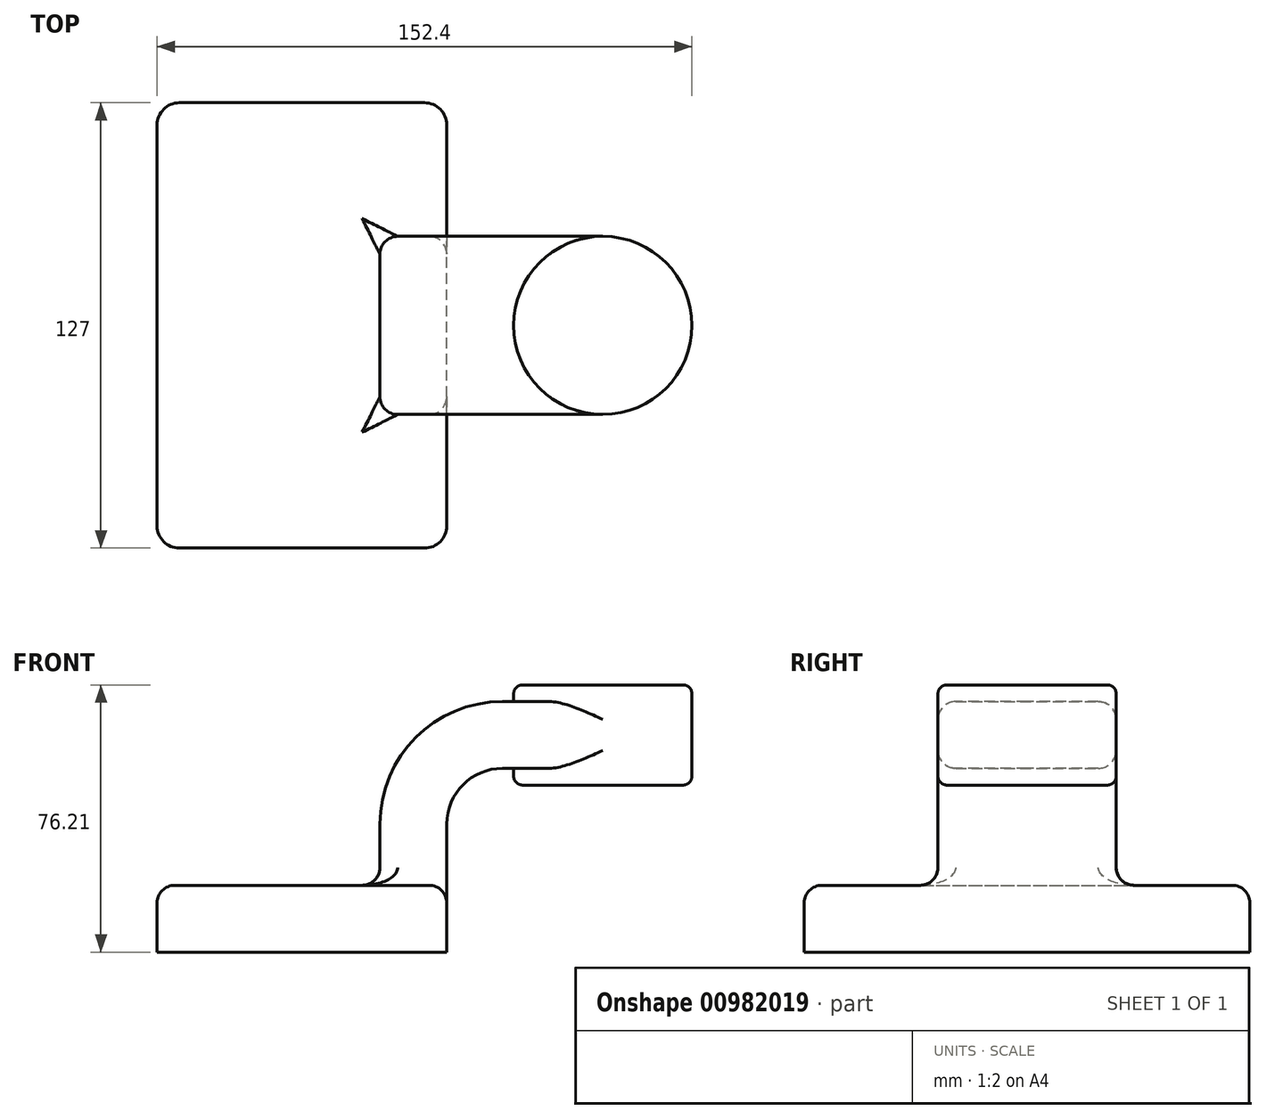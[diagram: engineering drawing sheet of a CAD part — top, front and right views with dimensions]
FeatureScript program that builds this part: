
annotation { "Feature Type Name" : "Feature", "Feature Type Description" : "" }
export const myFeature = defineFeature(function(context is Context, id is Id, definition is map)
    precondition{}
    {
        {
            var Q0;
            Q0=qCreatedBy(makeId("Front.planeOp"),FACE);
            var sketch = newSketch(context, id + "F0", { "sketchPlane" : qUnion([Q0])});
            skLineSegment(sketch, "E0.bottom", {"start": v(-41.28, -9.53) * mm, "end": v(41.28, -9.53) * mm});
            skLineSegment(sketch, "E0.top", {"start": v(-41.28, 9.52) * mm, "end": v(41.28, 9.52) * mm});
            skLineSegment(sketch, "E0.left", {"start": v(-41.28, -9.53) * mm, "end": v(-41.28, 9.52) * mm});
            skLineSegment(sketch, "E0.right", {"start": v(41.28, -9.53) * mm, "end": v(41.28, 9.52) * mm});
            skPoint(sketch, "E0.middle", {"position": v(0, 0) * mm});
            skLineSegment(sketch, "E1.bottom", {"start": v(111.12, 66.68) * mm, "end": v(60.32, 66.68) * mm});
            skLineSegment(sketch, "E1.top", {"start": v(111.12, 38.1) * mm, "end": v(60.32, 38.1) * mm});
            skLineSegment(sketch, "E1.left", {"start": v(111.12, 66.68) * mm, "end": v(111.12, 38.1) * mm});
            skLineSegment(sketch, "E1.right", {"start": v(60.32, 66.67) * mm, "end": v(60.32, 38.1) * mm});
            skPoint(sketch, "E1.middle", {"position": v(85.72, 52.39) * mm});
            skLineSegment(sketch, "E2", {"start": v(41.27, 9.52) * mm, "end": v(41.27, 27) * mm});
            skArc(sketch, "E3", {"start": v(41.27, 27) * mm, "mid": v(45.92, 38.23) * mm, "end": v(57.15, 42.88) * mm});
            skLineSegment(sketch, "E4", {"start": v(57.15, 42.88) * mm, "end": v(85.72, 42.88) * mm});
            skPoint(sketch, "E4.endSnap0", {"position": v(85.72, 38.1) * mm});
            skLineSegment(sketch, "E5.0", {"start": v(57.15, 61.93) * mm, "end": v(85.72, 61.93) * mm});
            skArc(sketch, "E5.1", {"start": v(22.23, 27) * mm, "mid": v(32.45, 51.7) * mm, "end": v(57.15, 61.93) * mm});
            skLineSegment(sketch, "E5.2", {"start": v(22.22, 9.52) * mm, "end": v(22.22, 27) * mm});
            skLineSegment(sketch, "E6", {"start": v(85.72, 66.68) * mm, "end": v(85.72, 38.1) * mm});
            skFitSpline(sketch, "E7", {"points": [v(-41.28, 9.53) * mm, v(57.15, 61.93) * mm], "startDerivative": vector(29.37, 69.56) * mm, "endDerivative": vector(135.05, -5.43) * mm});
            skSolve(sketch);
        }
        {
            var Q0;
            Q0=makeQuery(id+"F0.imprint","IMPRINT",FACE,{"disambiguationData":[TD([[makeQuery(id+"F0.imprint","IMPRINT",EDGE,{"derivedFrom":sQuery(id+"F0.wireOp",EDGE,"E0.bottom")}),1.0]])]});
            extrude(context, id + "F1", {"entities" : qUnion([Q0]), "endBound" : BoundingType.SYMMETRIC, "depth" : 127 * mm, "offsetDistance" : 25.4 * mm});
        }
        {
            var Q0;
            {var subQ1=sQuery(id+"F0.wireOp",EDGE,"E2");Q0=makeQuery(id+"F0.imprint","IMPRINT",FACE,{"disambiguationData":[TD([[makeQuery(id+"F0.imprint","IMPRINT",EDGE,{"derivedFrom":subQ1}),1.0]])]});}
            var Q1;
            {var subQ0=sQuery(id+"F0.wireOp",EDGE,"E5.0");var subQ1=sQuery(id+"F0.wireOp",EDGE,"E1.right");var subQ2=makeQuery(id+"F0.imprint","INTERSECT",VERTEX,{"derivedFrom":[subQ1,subQ0]});Q1=makeQuery(id+"F0.imprint","IMPRINT",FACE,{"disambiguationData":[TD([[makeQuery(id+"F0.imprint","IMPRINT",EDGE,{"disambiguationData":[TD([[subQ2,-1.0]])],"derivedFrom":subQ1}),1.0]])]});}
            extrude(context, id + "F2", {"entities" : qUnion([Q0, Q1]), "operationType" : NewBodyOperationType.ADD, "endBound" : BoundingType.SYMMETRIC, "depth" : 50.8 * mm, "offsetDistance" : 25.4 * mm});
        }
        {
            var Q0;
            Q0=makeQuery(id+"F0.imprint","IMPRINT",FACE,{"disambiguationData":[TD([[makeQuery(id+"F0.imprint","IMPRINT",EDGE,{"derivedFrom":sQuery(id+"F0.wireOp",EDGE,"E5.1")}),1.0]])]});
            extrude(context, id + "F3", {"entities" : qUnion([Q0]), "operationType" : NewBodyOperationType.ADD, "endBound" : BoundingType.SYMMETRIC, "depth" : 15.88 * mm, "offsetDistance" : 25.4 * mm});
        }
        {
            var Q0;
            {var subQ4=sQuery(id+"F0.wireOp",EDGE,"E1.left");Q0=makeQuery(id+"F0.imprint","IMPRINT",FACE,{"disambiguationData":[TD([[makeQuery(id+"F0.imprint","IMPRINT",EDGE,{"derivedFrom":subQ4}),-1.0]])]});}
            var Q1;
            Q1=sQuery(id+"F0.wireOp",EDGE,"E6");
            revolve(context, id + "F4", {"operationType" : NewBodyOperationType.ADD, "surfaceOperationType" : NewSurfaceOperationType.NEW, "entities" : qUnion([Q0]), "axis" : qUnion([Q1]), "revolveType" : RevolveType.FULL});
        }
        {
            var Q0;
            Q0=makeQuery(id+"F1.opExtrude","CAP_EDGE",EDGE,{"disambiguationData":[OSD([sQuery(id+"F0.wireOp",EDGE,"E0.right")])],"isStart":false});
            var Q1;
            Q1=makeQuery(id+"F1.opExtrude","CAP_EDGE",EDGE,{"disambiguationData":[OSD([sQuery(id+"F0.wireOp",EDGE,"E0.left")])],"isStart":false});
            var Q2;
            Q2=makeQuery(id+"F1.opExtrude","CAP_EDGE",EDGE,{"disambiguationData":[OSD([sQuery(id+"F0.wireOp",EDGE,"E0.right")])],"isStart":true});
            var Q3;
            Q3=makeQuery(id+"F1.opExtrude","CAP_EDGE",EDGE,{"disambiguationData":[OSD([sQuery(id+"F0.wireOp",EDGE,"E0.left")])],"isStart":true});
            fillet(context, id + "F5", {"entities" : qUnion([Q0, Q1, Q2, Q3]), "radius" : 6.35 * mm, "tangentPropagation" : true, "allowEdgeOverflow" : false});
        }
        {
            var Q0;
            Q0=makeQuery(id+"F3.opExtrude","CAP_EDGE",EDGE,{"disambiguationData":[OSD([sQuery(id+"F0.wireOp",EDGE,"E7")])],"isStart":false});
            var Q1;
            {var subQ3=sQuery(id+"F0.wireOp",EDGE,"E0.top");var subQ5=sQuery(id+"F0.wireOp",EDGE,"E0.right");var subQ6=sQuery(id+"F0.wireOp",EDGE,"E0.left");Q1=makeQuery(id+"F3.boolean.opBoolean","SPLIT",FACE,{"disambiguationData":[TD([makeQuery(id+"F1.opExtrude","CAP_FACE",FACE,{"disambiguationData":[OSD([sQuery(id+"F0.wireOp",EDGE,"E0.bottom"),subQ3,subQ6,subQ5])],"isStart":false})])],"derivedFrom":makeQuery(id+"F1.opExtrude","SWEPT_FACE",FACE,{"disambiguationData":[OSD([subQ3])]})});}
            var Q2;
            Q2=makeQuery(id+"F3.opExtrude","CAP_EDGE",EDGE,{"disambiguationData":[OSD([sQuery(id+"F0.wireOp",EDGE,"E7")])],"isStart":true});
            var Q3;
            {var subQ3=sQuery(id+"F0.wireOp",EDGE,"E0.top");var subQ4=sQuery(id+"F0.wireOp",EDGE,"E0.right");var subQ5=sQuery(id+"F0.wireOp",EDGE,"E0.left");Q3=makeQuery(id+"F3.boolean.opBoolean","SPLIT",FACE,{"disambiguationData":[TD([makeQuery(id+"F1.opExtrude","CAP_FACE",FACE,{"disambiguationData":[OSD([sQuery(id+"F0.wireOp",EDGE,"E0.bottom"),subQ3,subQ5,subQ4])],"isStart":true})])],"derivedFrom":makeQuery(id+"F1.opExtrude","SWEPT_FACE",FACE,{"disambiguationData":[OSD([subQ3])]})});}
            fillet(context, id + "F6", {"entities" : qUnion([Q0, Q1, Q2, Q3]), "radius" : 5.08 * mm, "tangentPropagation" : true, "allowEdgeOverflow" : false});
        }
        {
            var Q0;
            Q0=makeQuery(id+"F2.opExtrude","CAP_FACE",FACE,{"disambiguationData":[OSD([sQuery(id+"F0.wireOp",EDGE,"E0.top"),sQuery(id+"F0.wireOp",EDGE,"E2"),sQuery(id+"F0.wireOp",EDGE,"E3"),sQuery(id+"F0.wireOp",EDGE,"E4"),sQuery(id+"F0.wireOp",EDGE,"E5.0"),sQuery(id+"F0.wireOp",EDGE,"E5.1"),sQuery(id+"F0.wireOp",EDGE,"E5.2"),sQuery(id+"F0.wireOp",EDGE,"E6")])],"isStart":false});
            var Q1;
            Q1=makeQuery(id+"F2.opExtrude","CAP_FACE",FACE,{"disambiguationData":[OSD([sQuery(id+"F0.wireOp",EDGE,"E0.top"),sQuery(id+"F0.wireOp",EDGE,"E2"),sQuery(id+"F0.wireOp",EDGE,"E3"),sQuery(id+"F0.wireOp",EDGE,"E4"),sQuery(id+"F0.wireOp",EDGE,"E5.0"),sQuery(id+"F0.wireOp",EDGE,"E5.1"),sQuery(id+"F0.wireOp",EDGE,"E5.2"),sQuery(id+"F0.wireOp",EDGE,"E6")])],"isStart":true});
            fillet(context, id + "F7", {"entities" : qUnion([Q0, Q1]), "radius" : 5.08 * mm, "tangentPropagation" : true, "allowEdgeOverflow" : false});
        }
        {
            var Q0;
            Q0=makeQuery(id+"F4.opRevolve","SWEPT_EDGE",EDGE,{"disambiguationData":[OSD([sQuery(id+"F0.wireOp",EDGE,"E1.bottom"),sQuery(id+"F0.wireOp",EDGE,"E1.left")])]});
            fillet(context, id + "F8", {"entities" : qUnion([Q0]), "radius" : 2.54 * mm, "tangentPropagation" : true, "allowEdgeOverflow" : false});
        }
        {
            var Q0;
            Q0=makeQuery(id+"F4.opRevolve","SWEPT_FACE",FACE,{"disambiguationData":[OSD([sQuery(id+"F0.wireOp",EDGE,"E1.top")])]});
            fillet(context, id + "F9", {"entities" : qUnion([Q0]), "radius" : 2.54 * mm, "tangentPropagation" : true, "allowEdgeOverflow" : false});
        }
    });
